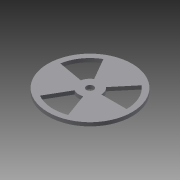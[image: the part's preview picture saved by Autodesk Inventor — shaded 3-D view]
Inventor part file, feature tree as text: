
AUTODESK INVENTOR PART (.ipt)
format: ipt  version: 2014 SP2 (Build 180246200, 246)  size: 104,960 bytes
history: native  units: mm
features: sketch x3, extrude x2, reference x2, hole x1
ambient origin geometry x8: Origin, YZ Plane, XZ Plane, XY Plane, X Axis, Y Axis, Z Axis, Center Point
bodies: Solid1 (feature_tree)
feature tree (8):
  extrude  "Extrusion1"  Depth=6.0mm
  extrude  "Extrusion3"  [1 undecoded]
  hole  "Hole1"  [1 undecoded]
  sketch  "Sketch1"  dims[d0=6.0mm d1=0.0mm d4=6.0mm]
  reference  "Reference1"
  sketch  "Sketch2"  dims[d5=4.0mm d6=0.0mm]
  reference  "Reference2"
  sketch  "Sketch3"  dims[d7=8.0mm d8=6.0mm d9=4.0mm d10=2.0mm d11=90.0deg d12=8.0mm d13=20.594885mm]
note: 2 required parameter values undecoded (feature->parameter linkage not recoverable at this tier; creation-order binding heuristic only, values carry confidence <= 0.55)
